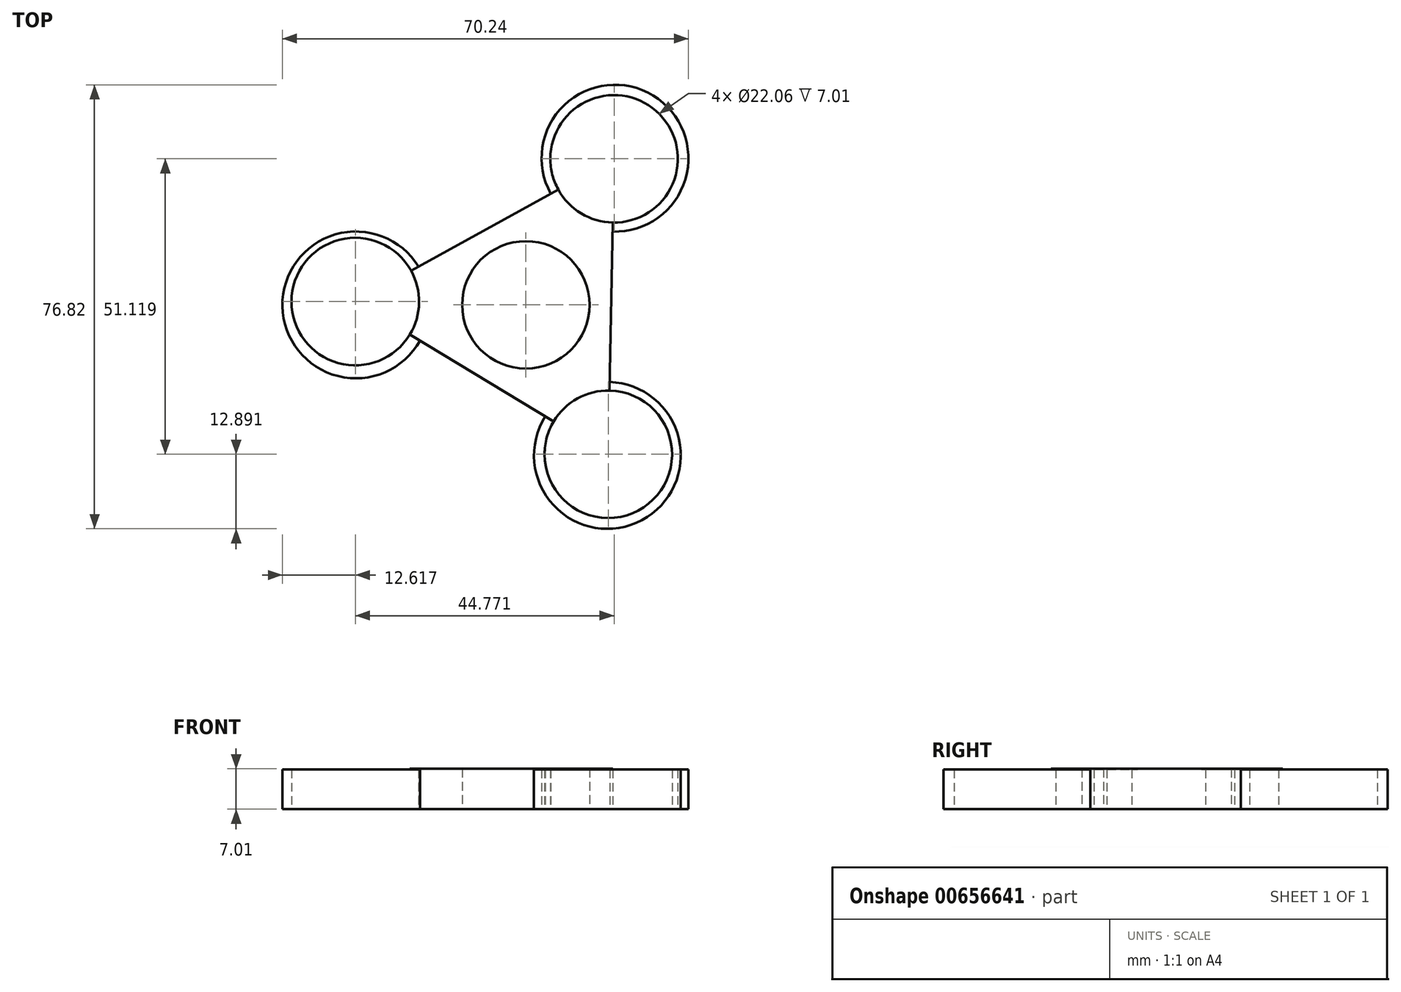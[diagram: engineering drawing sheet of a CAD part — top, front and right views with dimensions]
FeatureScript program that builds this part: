
annotation { "Feature Type Name" : "Feature", "Feature Type Description" : "" }
export const myFeature = defineFeature(function(context is Context, id is Id, definition is map)
    precondition{}
    {
        {
            var Q0;
            Q0=qCreatedBy(makeId("Top.planeOp"),FACE);
            var sketch = newSketch(context, id + "F0", { "sketchPlane" : qUnion([Q0])});
            skCircle(sketch, "E0.cCircle", {"center": v(0, 0) * mm, "radius": 14.76 * mm, "construction": true});
            skLineSegment(sketch, "E0.0", {"start": v(-29.51, 0.58) * mm, "end": v(15.26, 25.27) * mm});
            skLineSegment(sketch, "E0.1", {"start": v(15.26, 25.27) * mm, "end": v(14.26, -25.85) * mm});
            skLineSegment(sketch, "E0.2", {"start": v(14.26, -25.85) * mm, "end": v(-29.51, 0.58) * mm});
            skPoint(sketch, "E0.0.midPoint", {"position": v(-7.13, 12.92) * mm});
            skSolve(sketch);
        }
        {
            var Q0;
            Q0 = qSketchRegion(id + "F0", true);
            extrude(context, id + "F1", {"entities" : qUnion([Q0]), "depth" : 7 * mm, "offsetDistance" : 25.4 * mm});
        }
        {
            var Q0;
            Q0=sQuery(id+"F0.wireOp",VERTEX,"E0.cCircle.center");
            var Q1;
            Q1=makeQuery(id+"F1.opExtrude","SWEPT_BODY",BODY,{"disambiguationData":[OSD([sQuery(id+"F0.wireOp",EDGE,"E0.0"),sQuery(id+"F0.wireOp",EDGE,"E0.1"),sQuery(id+"F0.wireOp",EDGE,"E0.2")])]});
            hole(context, id + "F2", {"style" : HoleStyle.SIMPLE, "endStyle" : HoleEndStyle.THROUGH, "oppositeDirection" : true, "holeDiameter" : 22.06 * mm, "majorDiameter" : 6.35 * mm, "isTappedThrough" : true, "tappedDepth" : 12.7 * mm, "tapClearance" : 3, "locations" : qUnion([Q0]), "scope" : qUnion([Q1])});
        }
        {
            var Q0;
            Q0=qCreatedBy(makeId("Top.planeOp"),FACE);
            var sketch = newSketch(context, id + "F3", { "sketchPlane" : qUnion([Q0])});
            skCircle(sketch, "E1", {"center": v(14.1, -26.04) * mm, "radius": 12.7 * mm});
            skSolve(sketch);
        }
        {
            var Q0;
            Q0 = qSketchRegion(id + "F3", true);
            extrude(context, id + "F4", {"entities" : qUnion([Q0]), "operationType" : NewBodyOperationType.ADD, "depth" : 6.86 * mm, "offsetDistance" : 25.4 * mm});
        }
        {
            var Q0;
            Q0=qCreatedBy(makeId("Top.planeOp"),FACE);
            var sketch = newSketch(context, id + "F5", { "sketchPlane" : qUnion([Q0])});
            skCircle(sketch, "E2", {"center": v(15.41, 25.38) * mm, "radius": 12.7 * mm});
            skSolve(sketch);
        }
        {
            var Q0;
            Q0 = qSketchRegion(id + "F5", true);
            extrude(context, id + "F6", {"entities" : qUnion([Q0]), "operationType" : NewBodyOperationType.ADD, "depth" : 6.86 * mm, "offsetDistance" : 25.4 * mm});
        }
        {
            var Q0;
            Q0=qCreatedBy(makeId("Top.planeOp"),FACE);
            var sketch = newSketch(context, id + "F7", { "sketchPlane" : qUnion([Q0])});
            skCircle(sketch, "E3", {"center": v(-29.43, 0) * mm, "radius": 12.7 * mm});
            skSolve(sketch);
        }
        {
            var Q0;
            Q0 = qSketchRegion(id + "F7", true);
            extrude(context, id + "F8", {"entities" : qUnion([Q0]), "operationType" : NewBodyOperationType.ADD, "depth" : 6.86 * mm, "offsetDistance" : 25.4 * mm});
        }
        {
            var Q0;
            Q0=sQuery(id+"F0.wireOp",VERTEX,"E0.0.end");
            var Q1;
            Q1=makeQuery(id+"F1.opExtrude","SWEPT_BODY",BODY,{"disambiguationData":[OSD([sQuery(id+"F0.wireOp",EDGE,"E0.0"),sQuery(id+"F0.wireOp",EDGE,"E0.1"),sQuery(id+"F0.wireOp",EDGE,"E0.2")])]});
            hole(context, id + "F9", {"style" : HoleStyle.SIMPLE, "endStyle" : HoleEndStyle.THROUGH, "oppositeDirection" : true, "holeDiameter" : 22.06 * mm, "majorDiameter" : 6.35 * mm, "isTappedThrough" : true, "tappedDepth" : 12.7 * mm, "tapClearance" : 3, "locations" : qUnion([Q0]), "scope" : qUnion([Q1])});
        }
        {
            var Q0;
            Q0=sQuery(id+"F0.wireOp",VERTEX,"E0.1.end");
            var Q1;
            Q1=makeQuery(id+"F1.opExtrude","SWEPT_BODY",BODY,{"disambiguationData":[OSD([sQuery(id+"F0.wireOp",EDGE,"E0.0"),sQuery(id+"F0.wireOp",EDGE,"E0.1"),sQuery(id+"F0.wireOp",EDGE,"E0.2")])]});
            hole(context, id + "F10", {"style" : HoleStyle.SIMPLE, "endStyle" : HoleEndStyle.THROUGH, "oppositeDirection" : true, "holeDiameter" : 22.06 * mm, "majorDiameter" : 6.35 * mm, "isTappedThrough" : true, "tappedDepth" : 12.7 * mm, "tapClearance" : 3, "locations" : qUnion([Q0]), "scope" : qUnion([Q1])});
        }
        {
            var Q0;
            Q0=sQuery(id+"F0.wireOp",VERTEX,"E0.0.start");
            var Q1;
            Q1=makeQuery(id+"F1.opExtrude","SWEPT_BODY",BODY,{"disambiguationData":[OSD([sQuery(id+"F0.wireOp",EDGE,"E0.0"),sQuery(id+"F0.wireOp",EDGE,"E0.1"),sQuery(id+"F0.wireOp",EDGE,"E0.2")])]});
            hole(context, id + "F11", {"style" : HoleStyle.SIMPLE, "endStyle" : HoleEndStyle.THROUGH, "oppositeDirection" : true, "holeDiameter" : 22.06 * mm, "majorDiameter" : 6.35 * mm, "isTappedThrough" : true, "tappedDepth" : 12.7 * mm, "tapClearance" : 3, "locations" : qUnion([Q0]), "scope" : qUnion([Q1])});
        }
    });
